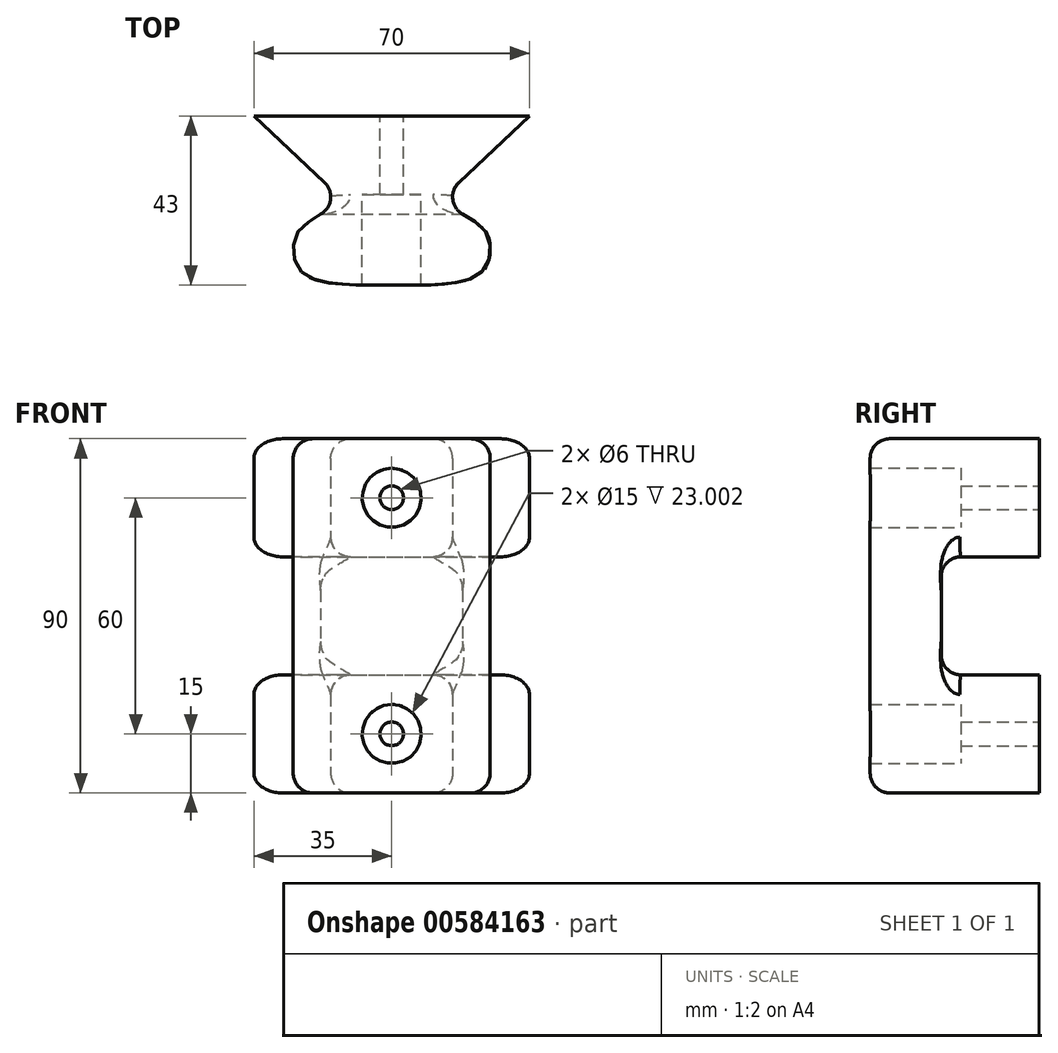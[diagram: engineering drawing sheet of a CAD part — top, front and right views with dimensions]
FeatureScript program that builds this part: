
annotation { "Feature Type Name" : "Feature", "Feature Type Description" : "" }
export const myFeature = defineFeature(function(context is Context, id is Id, definition is map)
    precondition{}
    {
        {
            var Q0;
            Q0=qCreatedBy(makeId("Top.planeOp"),FACE);
            var sketch = newSketch(context, id + "F0", { "sketchPlane" : qUnion([Q0])});
            skFitSpline(sketch, "E0", {"points": [v(0, -10) * mm, v(22.5, -7) * mm, v(25, 0) * mm, v(22.5, 5) * mm, v(0, 13) * mm, v(-22.5, 5) * mm, v(-25, 0) * mm, v(-22.5, -7) * mm, v(0, -10) * mm]});
            skLineSegment(sketch, "E1", {"start": v(0, 0) * mm, "end": v(-35, 33) * mm});
            skLineSegment(sketch, "E2", {"start": v(-35, 33) * mm, "end": v(35, 33) * mm});
            skLineSegment(sketch, "E3", {"start": v(35, 33) * mm, "end": v(0, 0) * mm});
            skSolve(sketch);
        }
        {
            var Q0;
            {var subQ0=sQuery(id+"F0.wireOp",EDGE,"E1");var subQ1=sQuery(id+"F0.wireOp",EDGE,"E0");var subQ2=makeQuery(id+"F0.imprint","INTERSECT",VERTEX,{"derivedFrom":[subQ1,subQ0]});Q0=makeQuery(id+"F0.imprint","IMPRINT",FACE,{"disambiguationData":[TD([[makeQuery(id+"F0.imprint","IMPRINT",EDGE,{"disambiguationData":[TD([[subQ2,-1.0]])],"derivedFrom":subQ1}),1.0]])]});}
            var Q1;
            {var subQ5=sQuery(id+"F0.wireOp",EDGE,"E2");Q1=makeQuery(id+"F0.imprint","IMPRINT",FACE,{"disambiguationData":[TD([[makeQuery(id+"F0.imprint","IMPRINT",EDGE,{"derivedFrom":subQ5}),-1.0]])]});}
            var Q2;
            {var subQ0=sQuery(id+"F0.wireOp",EDGE,"E1");var subQ1=sQuery(id+"F0.wireOp",EDGE,"E0");var subQ2=makeQuery(id+"F0.imprint","INTERSECT",VERTEX,{"derivedFrom":[subQ1,subQ0]});Q2=makeQuery(id+"F0.imprint","IMPRINT",FACE,{"disambiguationData":[TD([[makeQuery(id+"F0.imprint","IMPRINT",EDGE,{"disambiguationData":[TD([[subQ2,1.0]])],"derivedFrom":subQ1}),1.0]])]});}
            extrude(context, id + "F1", {"entities" : qUnion([Q0, Q1, Q2]), "depth" : 90 * mm, "offsetDistance" : 25 * mm});
        }
        {
            var Q0;
            Q0=makeQuery(id+"F1.opExtrude","SWEPT_EDGE",EDGE,{"disambiguationData":[OSD([sQuery(id+"F0.wireOp",EDGE,"E0"),sQuery(id+"F0.wireOp",EDGE,"E1")])]});
            var Q1;
            Q1=makeQuery(id+"F1.opExtrude","SWEPT_EDGE",EDGE,{"disambiguationData":[OSD([sQuery(id+"F0.wireOp",EDGE,"E0"),sQuery(id+"F0.wireOp",EDGE,"E3")])]});
            fillet(context, id + "F2", {"entities" : qUnion([Q0, Q1]), "radius" : 5 * mm, "tangentPropagation" : true, "allowEdgeOverflow" : false});
        }
        {
            var Q0;
            Q0=makeQuery(id+"F1.opExtrude","SWEPT_FACE",FACE,{"disambiguationData":[OSD([sQuery(id+"F0.wireOp",EDGE,"E2")])]});
            var sketch = newSketch(context, id + "F3", { "sketchPlane" : qUnion([Q0])});
            skCircle(sketch, "E4", {"center": v(0, 15) * mm, "radius": 3 * mm});
            skCircle(sketch, "E5", {"center": v(0, 75) * mm, "radius": 3 * mm});
            skCircle(sketch, "E6", {"center": v(0, 75) * mm, "radius": 7.5 * mm});
            skCircle(sketch, "E7", {"center": v(0, 15) * mm, "radius": 7.5 * mm});
            skSolve(sketch);
        }
        {
            var Q0;
            Q0=makeQuery(id+"F3.imprint","IMPRINT",FACE,{"disambiguationData":[TD([[makeQuery(id+"F3.imprint","IMPRINT",EDGE,{"derivedFrom":sQuery(id+"F3.wireOp",EDGE,"E4")}),1.0]])]});
            var Q1;
            Q1=makeQuery(id+"F3.imprint","IMPRINT",FACE,{"disambiguationData":[TD([[makeQuery(id+"F3.imprint","IMPRINT",EDGE,{"derivedFrom":sQuery(id+"F3.wireOp",EDGE,"E5")}),1.0]])]});
            var Q2;
            Q2=sQuery(id+"F3.wireOp",EDGE,"E4");
            var Q3;
            Q3=sQuery(id+"F3.wireOp",EDGE,"E5");
            extrude(context, id + "F4", {"entities" : qUnion([Q0, Q1]), "operationType" : NewBodyOperationType.REMOVE, "surfaceEntities" : qUnion([Q2, Q3]), "endBound" : BoundingType.THROUGH_ALL, "oppositeDirection" : true, "depth" : 25 * mm, "offsetDistance" : 25 * mm});
        }
        {
            var Q0;
            Q0=makeQuery(id+"F3.imprint","IMPRINT",FACE,{"disambiguationData":[TD([[makeQuery(id+"F3.imprint","IMPRINT",EDGE,{"derivedFrom":sQuery(id+"F3.wireOp",EDGE,"E5")}),-1.0]])]});
            var Q1;
            Q1=makeQuery(id+"F3.imprint","IMPRINT",FACE,{"disambiguationData":[TD([[makeQuery(id+"F3.imprint","IMPRINT",EDGE,{"derivedFrom":sQuery(id+"F3.wireOp",EDGE,"E4")}),-1.0]])]});
            var Q2;
            Q2=sQuery(id+"F3.wireOp",EDGE,"E6");
            var Q3;
            Q3=sQuery(id+"F3.wireOp",EDGE,"E7");
            extrude(context, id + "F5", {"entities" : qUnion([Q0, Q1]), "operationType" : NewBodyOperationType.REMOVE, "surfaceEntities" : qUnion([Q2, Q3]), "oppositeDirection" : true, "depth" : 90 * mm, "offsetDistance" : 25 * mm, "hasSecondDirection" : true, "secondDirectionOppositeDirection" : true, "secondDirectionDepth" : 20 * mm});
        }
        {
            var Q0;
            Q0=qCreatedBy(makeId("Right.planeOp"),FACE);
            cPlane(context, id + "F6", {"entities" : qUnion([Q0]), "cplaneType" : CPlaneType.OFFSET, "offset" : 40 * mm, "width" : 150 * mm, "height" : 150 * mm});
        }
        {
            var Q0;
            Q0=qCreatedBy(id+"F6.planeOp",FACE);
            var sketch = newSketch(context, id + "F7", { "sketchPlane" : qUnion([Q0])});
            skLineSegment(sketch, "E8.0", {"start": v(8.07, 0) * mm, "end": v(8.07, 90) * mm});
            skLineSegment(sketch, "E9.bottom", {"start": v(52.35, 30) * mm, "end": v(8.07, 30) * mm});
            skLineSegment(sketch, "E9.top", {"start": v(52.35, 60) * mm, "end": v(8.07, 60) * mm});
            skLineSegment(sketch, "E9.left", {"start": v(52.35, 30) * mm, "end": v(52.35, 60) * mm});
            skLineSegment(sketch, "E9.right", {"start": v(8.07, 30) * mm, "end": v(8.07, 60) * mm});
            skSolve(sketch);
        }
        {
            var Q0;
            Q0=makeQuery(id+"F7.imprint","IMPRINT",FACE,{"disambiguationData":[TD([[makeQuery(id+"F7.imprint","IMPRINT",EDGE,{"derivedFrom":sQuery(id+"F7.wireOp",EDGE,"E9.bottom")}),-1.0]])]});
            extrude(context, id + "F8", {"entities" : qUnion([Q0]), "operationType" : NewBodyOperationType.REMOVE, "endBound" : BoundingType.THROUGH_ALL, "oppositeDirection" : true, "depth" : 25 * mm, "offsetDistance" : 25 * mm});
        }
        {
            var Q0;
            Q0=makeQuery(id+"F8.boolean.opBoolean","COPY",EDGE,{"derivedFrom":makeQuery(id+"F8.opExtrude","SWEPT_EDGE",EDGE,{"disambiguationData":[OSD([sQuery(id+"F7.wireOp",EDGE,"E9.bottom"),sQuery(id+"F7.wireOp",EDGE,"E9.right")])]})});
            var Q1;
            Q1=makeQuery(id+"F8.boolean.opBoolean","COPY",EDGE,{"derivedFrom":makeQuery(id+"F8.opExtrude","SWEPT_EDGE",EDGE,{"disambiguationData":[OSD([sQuery(id+"F7.wireOp",EDGE,"E9.top"),sQuery(id+"F7.wireOp",EDGE,"E9.right")])]})});
            fillet(context, id + "F9", {"entities" : qUnion([Q0, Q1]), "radius" : 5 * mm, "tangentPropagation" : true, "allowEdgeOverflow" : false});
        }
        {
            var Q0;
            Q0=makeQuery(id+"F8.boolean.opBoolean","INTERSECT",EDGE,{"derivedFrom":[makeQuery(id+"F1.opExtrude","SWEPT_FACE",FACE,{"disambiguationData":[OSD([sQuery(id+"F0.wireOp",EDGE,"E1")])]}),makeQuery(id+"F8.opExtrude","SWEPT_FACE",FACE,{"disambiguationData":[OSD([sQuery(id+"F7.wireOp",EDGE,"E9.top")])]})]});
            var Q1;
            Q1=makeQuery(id+"F8.boolean.opBoolean","INTERSECT",EDGE,{"derivedFrom":[makeQuery(id+"F2.opFillet","BLEND_FACE",FACE,{"disambiguationData":[OSD([sQuery(id+"F0.wireOp",EDGE,"E0"),sQuery(id+"F0.wireOp",EDGE,"E1")])]}),makeQuery(id+"F8.opExtrude","SWEPT_FACE",FACE,{"disambiguationData":[OSD([sQuery(id+"F7.wireOp",EDGE,"E9.top")])]})]});
            var Q2;
            {var subQ0=sQuery(id+"F7.wireOp",EDGE,"E9.top");var subQ1=sQuery(id+"F0.wireOp",EDGE,"E1");var subQ2=sQuery(id+"F0.wireOp",EDGE,"E0");var subQ3=sQuery(id+"F7.wireOp",EDGE,"E9.right");Q2=makeQuery(id+"F9.opFillet","BLEND_EDGE",EDGE,{"blendedFrom":[makeQuery(id+"F8.boolean.opBoolean","COPY",EDGE,{"derivedFrom":makeQuery(id+"F8.opExtrude","SWEPT_EDGE",EDGE,{"disambiguationData":[OSD([subQ0,subQ3])]})}),makeQuery(id+"F8.boolean.opBoolean","SPLIT",FACE,{"disambiguationData":[TD([makeQuery(id+"F8.opExtrude","SWEPT_FACE",FACE,{"disambiguationData":[OSD([subQ0])]})])],"derivedFrom":makeQuery(id+"F2.opFillet","BLEND_FACE",FACE,{"disambiguationData":[OSD([subQ2,subQ1])]})})],"blendedInto":[makeQuery(id+"F8.boolean.opBoolean","SPLIT",FACE,{"disambiguationData":[TD([makeQuery(id+"F8.opExtrude","SWEPT_FACE",FACE,{"disambiguationData":[OSD([subQ0])]})])],"derivedFrom":makeQuery(id+"F2.opFillet","BLEND_FACE",FACE,{"disambiguationData":[OSD([subQ2,subQ1])]})})]});}
            var Q3;
            {var subQ0=sQuery(id+"F0.wireOp",EDGE,"E1");var subQ1=sQuery(id+"F7.wireOp",EDGE,"E9.bottom");var subQ2=sQuery(id+"F0.wireOp",EDGE,"E0");var subQ3=sQuery(id+"F7.wireOp",EDGE,"E9.right");Q3=makeQuery(id+"F9.opFillet","BLEND_EDGE",EDGE,{"blendedFrom":[makeQuery(id+"F8.boolean.opBoolean","COPY",EDGE,{"derivedFrom":makeQuery(id+"F8.opExtrude","SWEPT_EDGE",EDGE,{"disambiguationData":[OSD([subQ1,subQ3])]})}),makeQuery(id+"F8.boolean.opBoolean","SPLIT",FACE,{"disambiguationData":[TD([makeQuery(id+"F8.opExtrude","SWEPT_FACE",FACE,{"disambiguationData":[OSD([subQ1])]})])],"derivedFrom":makeQuery(id+"F2.opFillet","BLEND_FACE",FACE,{"disambiguationData":[OSD([subQ2,subQ0])]})})],"blendedInto":[makeQuery(id+"F8.boolean.opBoolean","SPLIT",FACE,{"disambiguationData":[TD([makeQuery(id+"F8.opExtrude","SWEPT_FACE",FACE,{"disambiguationData":[OSD([subQ1])]})])],"derivedFrom":makeQuery(id+"F2.opFillet","BLEND_FACE",FACE,{"disambiguationData":[OSD([subQ2,subQ0])]})})]});}
            var Q4;
            Q4=makeQuery(id+"F8.boolean.opBoolean","INTERSECT",EDGE,{"derivedFrom":[makeQuery(id+"F2.opFillet","BLEND_FACE",FACE,{"disambiguationData":[OSD([sQuery(id+"F0.wireOp",EDGE,"E0"),sQuery(id+"F0.wireOp",EDGE,"E1")])]}),makeQuery(id+"F8.opExtrude","SWEPT_FACE",FACE,{"disambiguationData":[OSD([sQuery(id+"F7.wireOp",EDGE,"E9.bottom")])]})]});
            var Q5;
            Q5=makeQuery(id+"F8.boolean.opBoolean","INTERSECT",EDGE,{"derivedFrom":[makeQuery(id+"F1.opExtrude","SWEPT_FACE",FACE,{"disambiguationData":[OSD([sQuery(id+"F0.wireOp",EDGE,"E1")])]}),makeQuery(id+"F8.opExtrude","SWEPT_FACE",FACE,{"disambiguationData":[OSD([sQuery(id+"F7.wireOp",EDGE,"E9.bottom")])]})]});
            var Q6;
            Q6=makeQuery(id+"F8.boolean.opBoolean","INTERSECT",EDGE,{"derivedFrom":[makeQuery(id+"F1.opExtrude","SWEPT_FACE",FACE,{"disambiguationData":[OSD([sQuery(id+"F0.wireOp",EDGE,"E3")])]}),makeQuery(id+"F8.opExtrude","SWEPT_FACE",FACE,{"disambiguationData":[OSD([sQuery(id+"F7.wireOp",EDGE,"E9.bottom")])]})]});
            var Q7;
            Q7=makeQuery(id+"F8.boolean.opBoolean","INTERSECT",EDGE,{"derivedFrom":[makeQuery(id+"F2.opFillet","BLEND_FACE",FACE,{"disambiguationData":[OSD([sQuery(id+"F0.wireOp",EDGE,"E0"),sQuery(id+"F0.wireOp",EDGE,"E3")])]}),makeQuery(id+"F8.opExtrude","SWEPT_FACE",FACE,{"disambiguationData":[OSD([sQuery(id+"F7.wireOp",EDGE,"E9.bottom")])]})]});
            var Q8;
            {var subQ0=sQuery(id+"F7.wireOp",EDGE,"E9.bottom");var subQ1=sQuery(id+"F0.wireOp",EDGE,"E0");var subQ2=sQuery(id+"F0.wireOp",EDGE,"E3");var subQ3=sQuery(id+"F7.wireOp",EDGE,"E9.right");Q8=makeQuery(id+"F9.opFillet","BLEND_EDGE",EDGE,{"blendedFrom":[makeQuery(id+"F8.boolean.opBoolean","COPY",EDGE,{"derivedFrom":makeQuery(id+"F8.opExtrude","SWEPT_EDGE",EDGE,{"disambiguationData":[OSD([subQ0,subQ3])]})}),makeQuery(id+"F8.boolean.opBoolean","SPLIT",FACE,{"disambiguationData":[TD([makeQuery(id+"F8.opExtrude","SWEPT_FACE",FACE,{"disambiguationData":[OSD([subQ0])]})])],"derivedFrom":makeQuery(id+"F2.opFillet","BLEND_FACE",FACE,{"disambiguationData":[OSD([subQ1,subQ2])]})})],"blendedInto":[makeQuery(id+"F8.boolean.opBoolean","SPLIT",FACE,{"disambiguationData":[TD([makeQuery(id+"F8.opExtrude","SWEPT_FACE",FACE,{"disambiguationData":[OSD([subQ0])]})])],"derivedFrom":makeQuery(id+"F2.opFillet","BLEND_FACE",FACE,{"disambiguationData":[OSD([subQ1,subQ2])]})})]});}
            var Q9;
            {var subQ0=sQuery(id+"F7.wireOp",EDGE,"E9.top");var subQ1=sQuery(id+"F0.wireOp",EDGE,"E3");var subQ2=sQuery(id+"F0.wireOp",EDGE,"E0");var subQ3=sQuery(id+"F7.wireOp",EDGE,"E9.right");Q9=makeQuery(id+"F9.opFillet","BLEND_EDGE",EDGE,{"blendedFrom":[makeQuery(id+"F8.boolean.opBoolean","COPY",EDGE,{"derivedFrom":makeQuery(id+"F8.opExtrude","SWEPT_EDGE",EDGE,{"disambiguationData":[OSD([subQ0,subQ3])]})}),makeQuery(id+"F8.boolean.opBoolean","SPLIT",FACE,{"disambiguationData":[TD([makeQuery(id+"F8.opExtrude","SWEPT_FACE",FACE,{"disambiguationData":[OSD([subQ0])]})])],"derivedFrom":makeQuery(id+"F2.opFillet","BLEND_FACE",FACE,{"disambiguationData":[OSD([subQ2,subQ1])]})})],"blendedInto":[makeQuery(id+"F8.boolean.opBoolean","SPLIT",FACE,{"disambiguationData":[TD([makeQuery(id+"F8.opExtrude","SWEPT_FACE",FACE,{"disambiguationData":[OSD([subQ0])]})])],"derivedFrom":makeQuery(id+"F2.opFillet","BLEND_FACE",FACE,{"disambiguationData":[OSD([subQ2,subQ1])]})})]});}
            var Q10;
            Q10=makeQuery(id+"F8.boolean.opBoolean","INTERSECT",EDGE,{"derivedFrom":[makeQuery(id+"F2.opFillet","BLEND_FACE",FACE,{"disambiguationData":[OSD([sQuery(id+"F0.wireOp",EDGE,"E0"),sQuery(id+"F0.wireOp",EDGE,"E3")])]}),makeQuery(id+"F8.opExtrude","SWEPT_FACE",FACE,{"disambiguationData":[OSD([sQuery(id+"F7.wireOp",EDGE,"E9.top")])]})]});
            var Q11;
            Q11=makeQuery(id+"F8.boolean.opBoolean","INTERSECT",EDGE,{"derivedFrom":[makeQuery(id+"F1.opExtrude","SWEPT_FACE",FACE,{"disambiguationData":[OSD([sQuery(id+"F0.wireOp",EDGE,"E3")])]}),makeQuery(id+"F8.opExtrude","SWEPT_FACE",FACE,{"disambiguationData":[OSD([sQuery(id+"F7.wireOp",EDGE,"E9.top")])]})]});
            var Q12;
            Q12=makeQuery(id+"F1.opExtrude","CAP_EDGE",EDGE,{"disambiguationData":[OSD([sQuery(id+"F0.wireOp",EDGE,"E3")])],"isStart":true});
            var Q13;
            {var subQ0=sQuery(id+"F0.wireOp",EDGE,"E3");var subQ1=sQuery(id+"F0.wireOp",EDGE,"E0");Q13=makeQuery(id+"F2.opFillet","BLEND_EDGE",EDGE,{"blendedFrom":[makeQuery(id+"F1.opExtrude","SWEPT_EDGE",EDGE,{"disambiguationData":[OSD([subQ1,subQ0])]}),makeQuery(id+"F1.opExtrude","CAP_FACE",FACE,{"disambiguationData":[OSD([subQ1,sQuery(id+"F0.wireOp",EDGE,"E1"),sQuery(id+"F0.wireOp",EDGE,"E2"),subQ0])],"isStart":true})],"blendedInto":[makeQuery(id+"F1.opExtrude","CAP_FACE",FACE,{"disambiguationData":[OSD([subQ1,sQuery(id+"F0.wireOp",EDGE,"E1"),sQuery(id+"F0.wireOp",EDGE,"E2"),subQ0])],"isStart":true})]});}
            var Q14;
            {var subQ0=sQuery(id+"F0.wireOp",EDGE,"E1");var subQ1=sQuery(id+"F0.wireOp",EDGE,"E0");Q14=makeQuery(id+"F2.opFillet","BLEND_EDGE",EDGE,{"blendedFrom":[makeQuery(id+"F1.opExtrude","SWEPT_EDGE",EDGE,{"disambiguationData":[OSD([subQ1,subQ0])]}),makeQuery(id+"F1.opExtrude","CAP_FACE",FACE,{"disambiguationData":[OSD([subQ1,subQ0,sQuery(id+"F0.wireOp",EDGE,"E2"),sQuery(id+"F0.wireOp",EDGE,"E3")])],"isStart":true})],"blendedInto":[makeQuery(id+"F1.opExtrude","CAP_FACE",FACE,{"disambiguationData":[OSD([subQ1,subQ0,sQuery(id+"F0.wireOp",EDGE,"E2"),sQuery(id+"F0.wireOp",EDGE,"E3")])],"isStart":true})]});}
            var Q15;
            Q15=makeQuery(id+"F1.opExtrude","CAP_EDGE",EDGE,{"disambiguationData":[OSD([sQuery(id+"F0.wireOp",EDGE,"E1")])],"isStart":true});
            var Q16;
            Q16=makeQuery(id+"F1.opExtrude","CAP_EDGE",EDGE,{"disambiguationData":[OSD([sQuery(id+"F0.wireOp",EDGE,"E0")])],"isStart":true});
            var Q17;
            Q17=makeQuery(id+"F1.opExtrude","CAP_EDGE",EDGE,{"disambiguationData":[OSD([sQuery(id+"F0.wireOp",EDGE,"E3")])],"isStart":false});
            var Q18;
            {var subQ0=sQuery(id+"F0.wireOp",EDGE,"E3");var subQ1=sQuery(id+"F0.wireOp",EDGE,"E0");Q18=makeQuery(id+"F2.opFillet","BLEND_EDGE",EDGE,{"blendedFrom":[makeQuery(id+"F1.opExtrude","SWEPT_EDGE",EDGE,{"disambiguationData":[OSD([subQ1,subQ0])]}),makeQuery(id+"F1.opExtrude","CAP_FACE",FACE,{"disambiguationData":[OSD([subQ1,sQuery(id+"F0.wireOp",EDGE,"E1"),sQuery(id+"F0.wireOp",EDGE,"E2"),subQ0])],"isStart":false})],"blendedInto":[makeQuery(id+"F1.opExtrude","CAP_FACE",FACE,{"disambiguationData":[OSD([subQ1,sQuery(id+"F0.wireOp",EDGE,"E1"),sQuery(id+"F0.wireOp",EDGE,"E2"),subQ0])],"isStart":false})]});}
            var Q19;
            {var subQ0=sQuery(id+"F0.wireOp",EDGE,"E1");var subQ1=sQuery(id+"F0.wireOp",EDGE,"E0");Q19=makeQuery(id+"F2.opFillet","BLEND_EDGE",EDGE,{"blendedFrom":[makeQuery(id+"F1.opExtrude","SWEPT_EDGE",EDGE,{"disambiguationData":[OSD([subQ1,subQ0])]}),makeQuery(id+"F1.opExtrude","CAP_FACE",FACE,{"disambiguationData":[OSD([subQ1,subQ0,sQuery(id+"F0.wireOp",EDGE,"E2"),sQuery(id+"F0.wireOp",EDGE,"E3")])],"isStart":false})],"blendedInto":[makeQuery(id+"F1.opExtrude","CAP_FACE",FACE,{"disambiguationData":[OSD([subQ1,subQ0,sQuery(id+"F0.wireOp",EDGE,"E2"),sQuery(id+"F0.wireOp",EDGE,"E3")])],"isStart":false})]});}
            var Q20;
            Q20=makeQuery(id+"F1.opExtrude","CAP_EDGE",EDGE,{"disambiguationData":[OSD([sQuery(id+"F0.wireOp",EDGE,"E1")])],"isStart":false});
            var Q21;
            Q21=makeQuery(id+"F1.opExtrude","CAP_EDGE",EDGE,{"disambiguationData":[OSD([sQuery(id+"F0.wireOp",EDGE,"E0")])],"isStart":false});
            fillet(context, id + "F10", {"entities" : qUnion([Q0, Q1, Q2, Q3, Q4, Q5, Q6, Q7, Q8, Q9, Q10, Q11, Q12, Q13, Q14, Q15, Q16, Q17, Q18, Q19, Q20, Q21]), "radius" : 5 * mm, "allowEdgeOverflow" : false});
        }
    });
